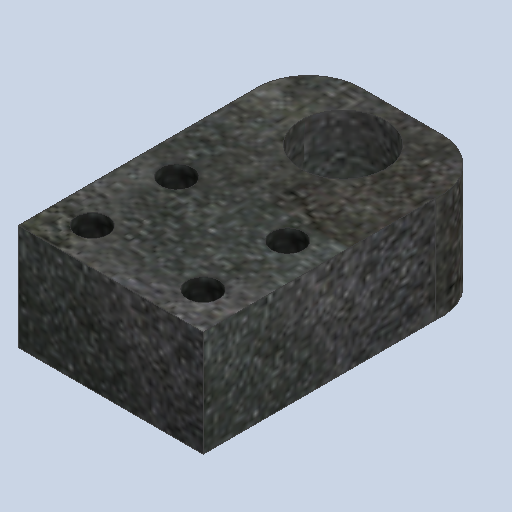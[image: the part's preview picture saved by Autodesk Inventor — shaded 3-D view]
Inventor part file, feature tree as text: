
AUTODESK INVENTOR PART (.ipt)
format: ipt  version: 2023.2 (Build 272271000, 271)  size: 357,888 bytes
history: native  units: mm
features: extrude x2, sketch x2
ambient origin geometry x8: Origin, YZ Plane, XZ Plane, XY Plane, X Axis, Y Axis, Z Axis, Center Point
bodies: Solid1 (feature_tree)
feature tree (4):
  extrude  "Extrusion1"  Depth=55.0mm
  extrude  "Extrusion2"  Depth=13.0mm
  sketch  "Sketch1"  dims[d0=35.0mm d1=55.0mm]
  sketch  "Sketch2"  dims[d5=11.0mm d7=11.0mm d9=11.0mm d11=11.0mm d13=7.0mm d15=23.0mm d16=21.0mm d17=10.5mm d18=44.0mm d19=16.0mm d20=44.0mm d25=10.0mm d26=10.0mm d27=7.0mm d28=0.0mm d29=16.0mm d30=6.0mm d31=6.0mm d32=6.0mm d33=6.0mm d34=7.0mm d35=23.0mm d36=21.0mm d37=10.5mm d38=13.0mm d39=0.0mm]
